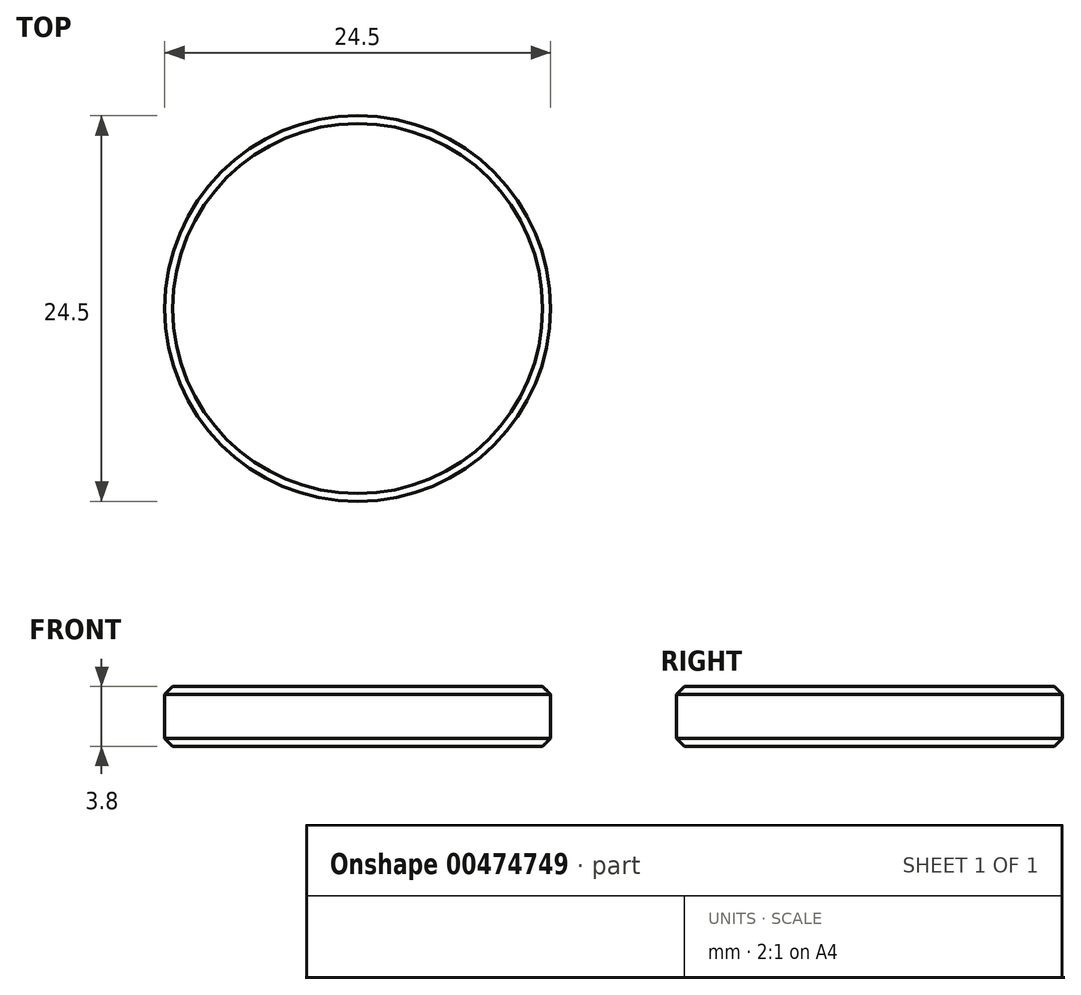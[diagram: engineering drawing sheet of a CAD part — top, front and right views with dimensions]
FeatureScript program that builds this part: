
annotation { "Feature Type Name" : "Feature", "Feature Type Description" : "" }
export const myFeature = defineFeature(function(context is Context, id is Id, definition is map)
    precondition{}
    {
        {
            var Q0;
            Q0=qCreatedBy(makeId("Top.planeOp"),FACE);
            var sketch = newSketch(context, id + "F0", { "sketchPlane" : qUnion([Q0])});
            skCircle(sketch, "E0", {"center": v(0, 0) * mm, "radius": 12.25 * mm});
            skSolve(sketch);
        }
        {
            var Q0;
            Q0 = qSketchRegion(id + "F0", true);
            extrude(context, id + "F1", {"entities" : qUnion([Q0]), "depth" : 3.8 * mm, "offsetDistance" : 25 * mm});
        }
        {
            var Q0;
            Q0=makeQuery(id+"F1.opExtrude","CAP_EDGE",EDGE,{"disambiguationData":[OSD([sQuery(id+"F0.wireOp",EDGE,"E0")])],"isStart":false});
            var Q1;
            Q1=makeQuery(id+"F1.opExtrude","CAP_EDGE",EDGE,{"disambiguationData":[OSD([sQuery(id+"F0.wireOp",EDGE,"E0")])],"isStart":true});
            chamfer(context, id + "F2", {"entities" : qUnion([Q0, Q1]), "width" : 0.5 * mm, "tangentPropagation" : true});
        }
    });
